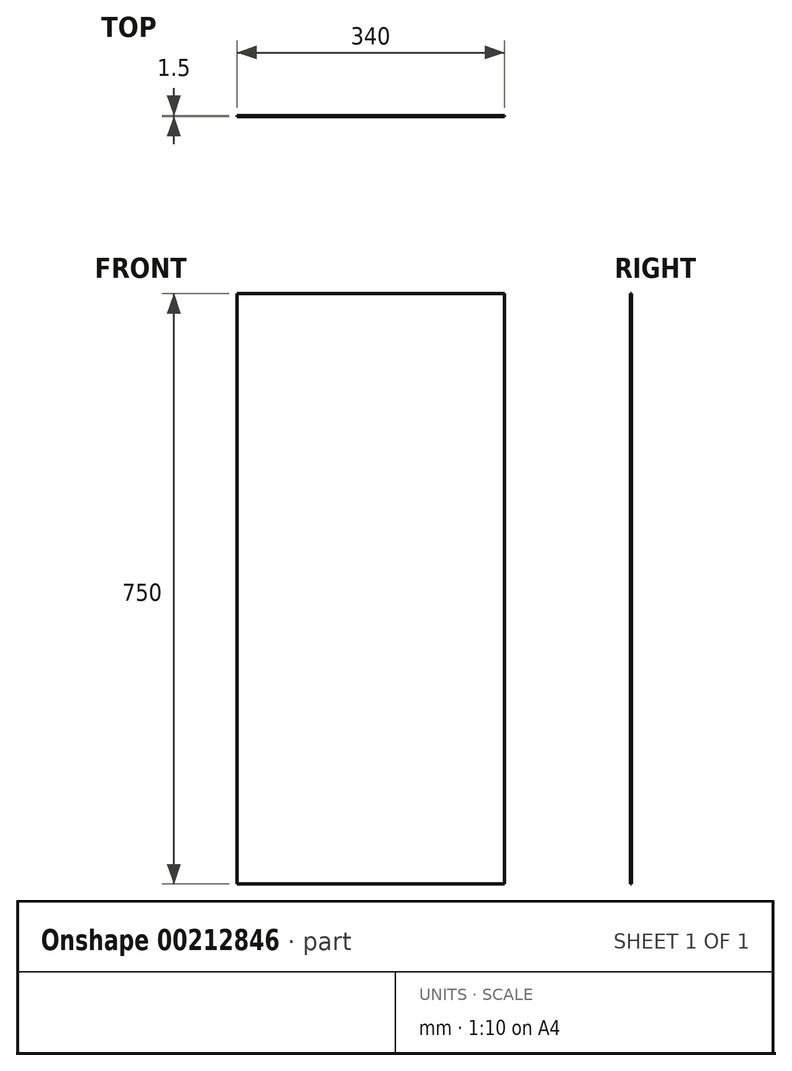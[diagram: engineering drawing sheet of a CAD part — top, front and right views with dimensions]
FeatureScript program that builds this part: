
annotation { "Feature Type Name" : "Feature", "Feature Type Description" : "" }
export const myFeature = defineFeature(function(context is Context, id is Id, definition is map)
    precondition{}
    {
        {
            var Q0;
            Q0=qCreatedBy(makeId("Front.planeOp"),FACE);
            var sketch = newSketch(context, id + "F0", { "sketchPlane" : qUnion([Q0])});
            skLineSegment(sketch, "E0.bottom", {"start": v(-170, 375) * mm, "end": v(170, 375) * mm});
            skLineSegment(sketch, "E0.top", {"start": v(-170, -375) * mm, "end": v(170, -375) * mm});
            skLineSegment(sketch, "E0.left", {"start": v(-170, 375) * mm, "end": v(-170, -375) * mm});
            skLineSegment(sketch, "E0.right", {"start": v(170, 375) * mm, "end": v(170, -375) * mm});
            skSolve(sketch);
        }
        {
            var Q0;
            Q0=makeQuery(id+"F0.imprint","IMPRINT",FACE,{"disambiguationData":[TD([[makeQuery(id+"F0.imprint","IMPRINT",EDGE,{"derivedFrom":sQuery(id+"F0.wireOp",EDGE,"E0.bottom")}),-1.0]])]});
            extrude(context, id + "F1", {"entities" : qUnion([Q0]), "depth" : 1.5 * mm});
        }
    });
